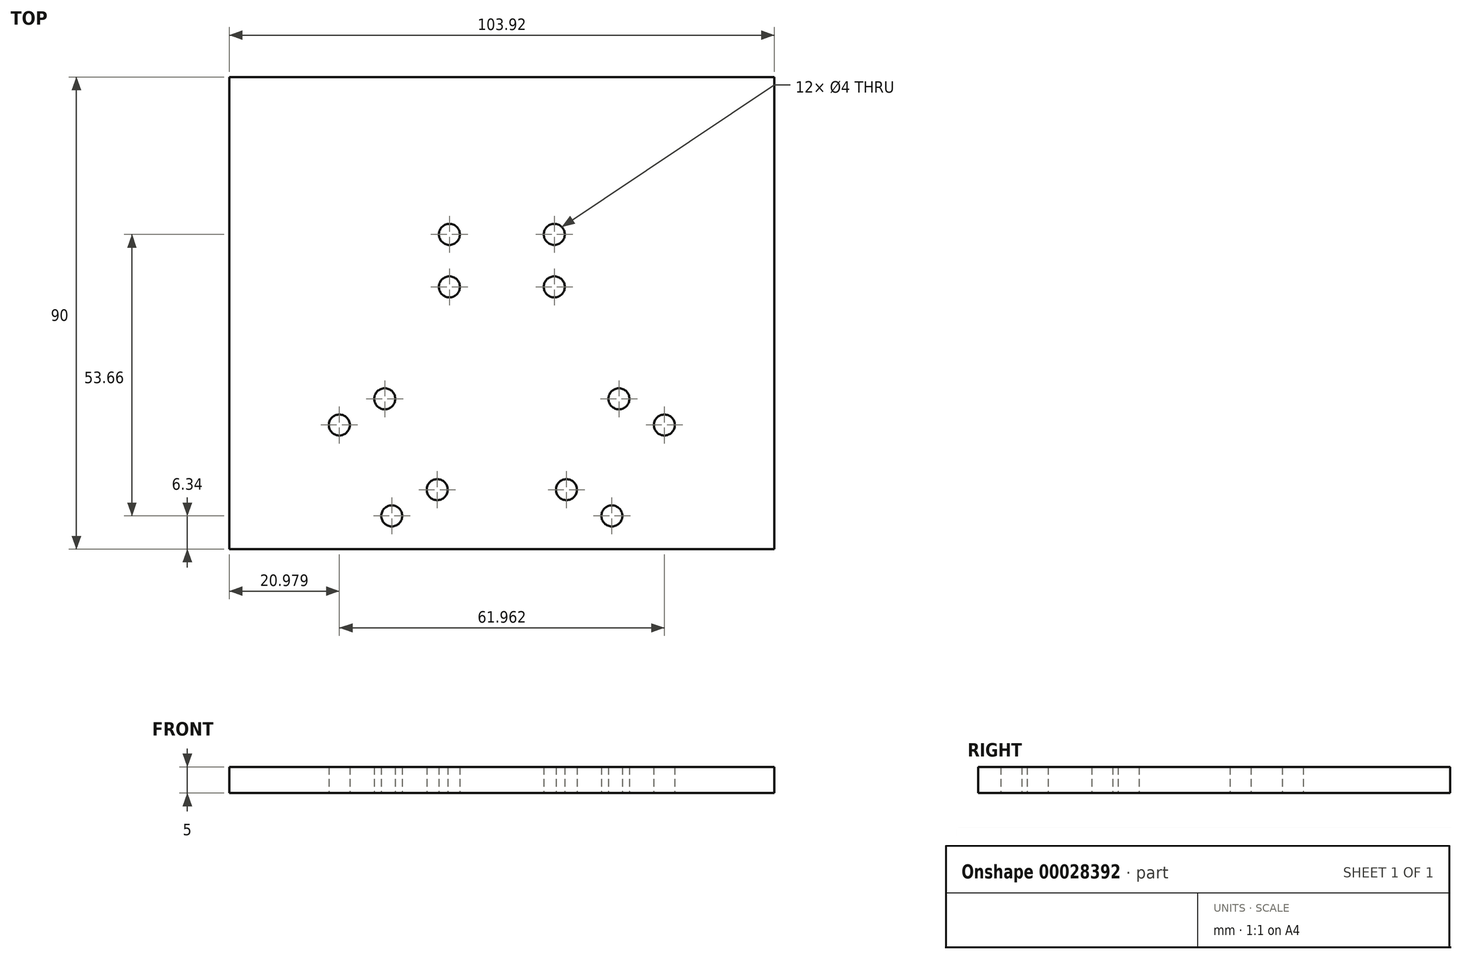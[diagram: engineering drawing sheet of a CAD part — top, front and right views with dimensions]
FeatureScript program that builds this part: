
annotation { "Feature Type Name" : "Feature", "Feature Type Description" : "" }
export const myFeature = defineFeature(function(context is Context, id is Id, definition is map)
    precondition{}
    {
        {
            var Q0;
            Q0=qCreatedBy(makeId("Top.planeOp"),FACE);
            var sketch = newSketch(context, id + "F0", { "sketchPlane" : qUnion([Q0])});
            skLineSegment(sketch, "E0", {"start": v(0, 0) * mm, "end": v(0, 60) * mm, "construction": true});
            skLineSegment(sketch, "E1", {"start": v(0, 0) * mm, "end": v(-51.96, -30) * mm, "construction": true});
            skLineSegment(sketch, "E2", {"start": v(0, 0) * mm, "end": v(51.96, -30) * mm, "construction": true});
            skLineSegment(sketch, "E3", {"start": v(-51.96, -30) * mm, "end": v(51.96, -30) * mm});
            skLineSegment(sketch, "E4", {"start": v(0, 60) * mm, "end": v(51.96, 60) * mm});
            skLineSegment(sketch, "E5", {"start": v(51.96, 60) * mm, "end": v(51.96, -30) * mm});
            skLineSegment(sketch, "E6", {"start": v(0, 60) * mm, "end": v(-51.96, 60) * mm});
            skLineSegment(sketch, "E7", {"start": v(-51.96, 60) * mm, "end": v(-51.96, -30) * mm});
            skLineSegment(sketch, "E8", {"start": v(-10, 60) * mm, "end": v(-10, 5.77) * mm, "construction": true});
            skLineSegment(sketch, "E9", {"start": v(10, 60) * mm, "end": v(10, 5.77) * mm, "construction": true});
            skLineSegment(sketch, "E10", {"start": v(-51.96, -18.45) * mm, "end": v(-10, 5.77) * mm, "construction": true});
            skLineSegment(sketch, "E11", {"start": v(51.96, -18.45) * mm, "end": v(10, 5.77) * mm, "construction": true});
            skLineSegment(sketch, "E12", {"start": v(-31.96, -30) * mm, "end": v(0, -11.55) * mm, "construction": true});
            skLineSegment(sketch, "E13", {"start": v(31.96, -30) * mm, "end": v(0, -11.55) * mm, "construction": true});
            skCircle(sketch, "E14", {"center": v(10, 30) * mm, "radius": 2 * mm});
            skCircle(sketch, "E15", {"center": v(10, 20) * mm, "radius": 2 * mm});
            skCircle(sketch, "E16", {"center": v(-10, 30) * mm, "radius": 2 * mm});
            skCircle(sketch, "E17", {"center": v(-10, 20) * mm, "radius": 2 * mm});
            skCircle(sketch, "E18.1.0", {"center": v(-30.98, -6.34) * mm, "radius": 2 * mm});
            skCircle(sketch, "E18.1.1", {"center": v(-20.98, -23.66) * mm, "radius": 2 * mm});
            skCircle(sketch, "E18.1.2", {"center": v(-12.32, -18.66) * mm, "radius": 2 * mm});
            skCircle(sketch, "E18.1.3", {"center": v(-22.32, -1.34) * mm, "radius": 2 * mm});
            skCircle(sketch, "E18.2.0", {"center": v(20.98, -23.66) * mm, "radius": 2 * mm});
            skCircle(sketch, "E18.2.1", {"center": v(30.98, -6.34) * mm, "radius": 2 * mm});
            skCircle(sketch, "E18.2.2", {"center": v(22.32, -1.34) * mm, "radius": 2 * mm});
            skCircle(sketch, "E18.2.3", {"center": v(12.32, -18.66) * mm, "radius": 2 * mm});
            skPoint(sketch, "E18.center", {"position": v(0, 0) * mm});
            skSolve(sketch);
        }
        {
            var Q0;
            Q0 = qSketchRegion(id + "F0", true);
            extrude(context, id + "F1", {"entities" : qUnion([Q0]), "depth" : 5 * mm});
        }
    });
